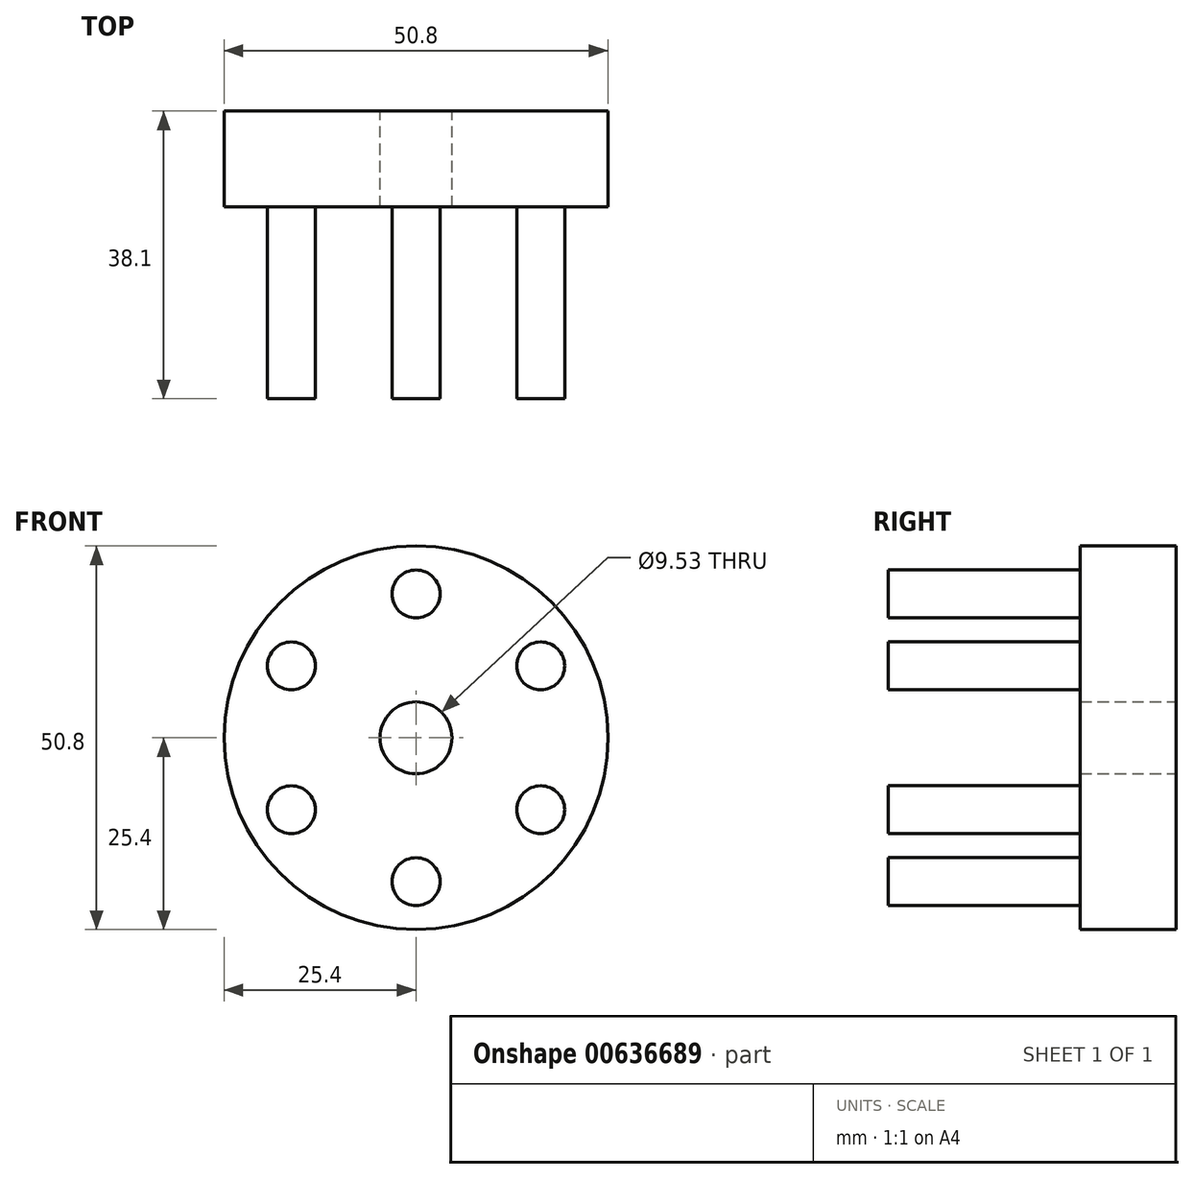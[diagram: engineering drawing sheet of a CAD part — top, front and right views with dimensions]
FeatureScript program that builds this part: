
annotation { "Feature Type Name" : "Feature", "Feature Type Description" : "" }
export const myFeature = defineFeature(function(context is Context, id is Id, definition is map)
    precondition{}
    {
        {
            var Q0;
            Q0=qCreatedBy(makeId("Front.planeOp"),FACE);
            var sketch = newSketch(context, id + "F0", { "sketchPlane" : qUnion([Q0])});
            skCircle(sketch, "E0", {"center": v(0, 0) * mm, "radius": 25.4 * mm});
            skSolve(sketch);
        }
        {
            var Q0;
            Q0=makeQuery(id+"F0.imprint","IMPRINT",FACE,{"disambiguationData":[TD([[makeQuery(id+"F0.imprint","IMPRINT",EDGE,{"derivedFrom":sQuery(id+"F0.wireOp",EDGE,"E0")}),1.0]])]});
            extrude(context, id + "F1", {"entities" : qUnion([Q0]), "depth" : 12.7 * mm, "offsetDistance" : 25.4 * mm});
        }
        {
            var Q0;
            Q0=makeQuery(id+"F1.opExtrude","CAP_FACE",FACE,{"disambiguationData":[OSD([sQuery(id+"F0.wireOp",EDGE,"E0")])],"isStart":false});
            var sketch = newSketch(context, id + "F2", { "sketchPlane" : qUnion([Q0])});
            skLineSegment(sketch, "E1", {"start": v(0, 25.4) * mm, "end": v(0, 19.05) * mm, "construction": true});
            skCircle(sketch, "E2", {"center": v(0, 19.05) * mm, "radius": 3.18 * mm});
            skCircle(sketch, "E3.1.0", {"center": v(-16.5, 9.53) * mm, "radius": 3.18 * mm});
            skCircle(sketch, "E3.2.0", {"center": v(-16.5, -9.52) * mm, "radius": 3.18 * mm});
            skCircle(sketch, "E3.3.0", {"center": v(0, -19.05) * mm, "radius": 3.18 * mm});
            skCircle(sketch, "E3.4.0", {"center": v(16.5, -9.53) * mm, "radius": 3.18 * mm});
            skCircle(sketch, "E3.5.0", {"center": v(16.5, 9.53) * mm, "radius": 3.18 * mm});
            skPoint(sketch, "E3.center", {"position": v(0, 0) * mm});
            skSolve(sketch);
        }
        {
            var Q0;
            Q0=makeQuery(id+"F2.imprint","IMPRINT",FACE,{"disambiguationData":[TD([[makeQuery(id+"F2.imprint","IMPRINT",EDGE,{"derivedFrom":sQuery(id+"F2.wireOp",EDGE,"E3.1.0")}),1.0]])]});
            var Q1;
            Q1=makeQuery(id+"F2.imprint","IMPRINT",FACE,{"disambiguationData":[TD([[makeQuery(id+"F2.imprint","IMPRINT",EDGE,{"derivedFrom":sQuery(id+"F2.wireOp",EDGE,"E2")}),1.0]])]});
            var Q2;
            Q2=makeQuery(id+"F2.imprint","IMPRINT",FACE,{"disambiguationData":[TD([[makeQuery(id+"F2.imprint","IMPRINT",EDGE,{"derivedFrom":sQuery(id+"F2.wireOp",EDGE,"E3.4.0")}),1.0]])]});
            var Q3;
            Q3=makeQuery(id+"F2.imprint","IMPRINT",FACE,{"disambiguationData":[TD([[makeQuery(id+"F2.imprint","IMPRINT",EDGE,{"derivedFrom":sQuery(id+"F2.wireOp",EDGE,"E3.2.0")}),1.0]])]});
            var Q4;
            Q4=makeQuery(id+"F2.imprint","IMPRINT",FACE,{"disambiguationData":[TD([[makeQuery(id+"F2.imprint","IMPRINT",EDGE,{"derivedFrom":sQuery(id+"F2.wireOp",EDGE,"E3.3.0")}),1.0]])]});
            var Q5;
            Q5=makeQuery(id+"F2.imprint","IMPRINT",FACE,{"disambiguationData":[TD([[makeQuery(id+"F2.imprint","IMPRINT",EDGE,{"derivedFrom":sQuery(id+"F2.wireOp",EDGE,"E3.5.0")}),1.0]])]});
            extrude(context, id + "F3", {"entities" : qUnion([Q0, Q1, Q2, Q3, Q4, Q5]), "operationType" : NewBodyOperationType.ADD, "depth" : 25.4 * mm, "offsetDistance" : 25.4 * mm});
        }
        {
            var Q0;
            Q0=makeQuery(id+"F1.opExtrude","CAP_FACE",FACE,{"disambiguationData":[OSD([sQuery(id+"F0.wireOp",EDGE,"E0")])],"isStart":true});
            var sketch = newSketch(context, id + "F4", { "sketchPlane" : qUnion([Q0])});
            skCircle(sketch, "E4", {"center": v(0, 0) * mm, "radius": 4.76 * mm});
            skSolve(sketch);
        }
        {
            var Q0;
            Q0=makeQuery(id+"F4.imprint","IMPRINT",FACE,{"disambiguationData":[TD([[makeQuery(id+"F4.imprint","IMPRINT",EDGE,{"derivedFrom":sQuery(id+"F4.wireOp",EDGE,"E4")}),1.0]])]});
            extrude(context, id + "F5", {"entities" : qUnion([Q0]), "operationType" : NewBodyOperationType.REMOVE, "oppositeDirection" : true, "depth" : 12.7 * mm, "offsetDistance" : 25.4 * mm});
        }
    });
